# Revit family: Coifa Tube
name_source: partatom
category: Equipamento mecânico
revit_build: Autodesk Revit 2014 (Build: 20130308_1515(x64)
units: mm (PartAtom-declared; Revit-internal decimal feet)

## types (2) — shared parameters
Altura Total (Min. 1,025m / Máx. 1,250m) = 1.25
Atendimento ao Cliente = http://www.tramontina.com.br
Classe da Construção = CLASSE I
Descrição = COIFA DE ILHA TUBE ISLA 35
Desenvolvedor da Biblioteca = Studio BIM
Disjuntor Termomagnético = 10 A
Fabricante = Tramontina
Frequência = 60 Hz
Grau de Proteção = IPX0
Iluminação = Lâmpadas Leds [3 x 1 W - 12 V]
Linha = Tube
Nível de Ruído = 76 db(A) - cfe. Norma EN 60704
Peso Bruto (Kg) = 28
Peso Líquido (Kg) = 22
Produto = COIFA DE ILHA TUBE ISLA 35
Segmento = Residencial
Site do Desenvolvedor = www.studiobim.arq.br
URL = http://www.tramontina.com.br
Vazão Máxima = 830 m3/h - cfe. Norma IEC 61591

## per-type parameters (varying)
| type | Código da Peça | Modelo | Potência Elétrica | Potência do Motor | Tensão |
| 110 Volts | 94833/110 | 94833/110 | 333 W | 330 W | 127 V |
| 220 Volts | 94833/220
94833/220
94833/220 | 94833/220
94833/220
94833/220 | 348 W | 345 W | 220 V |
